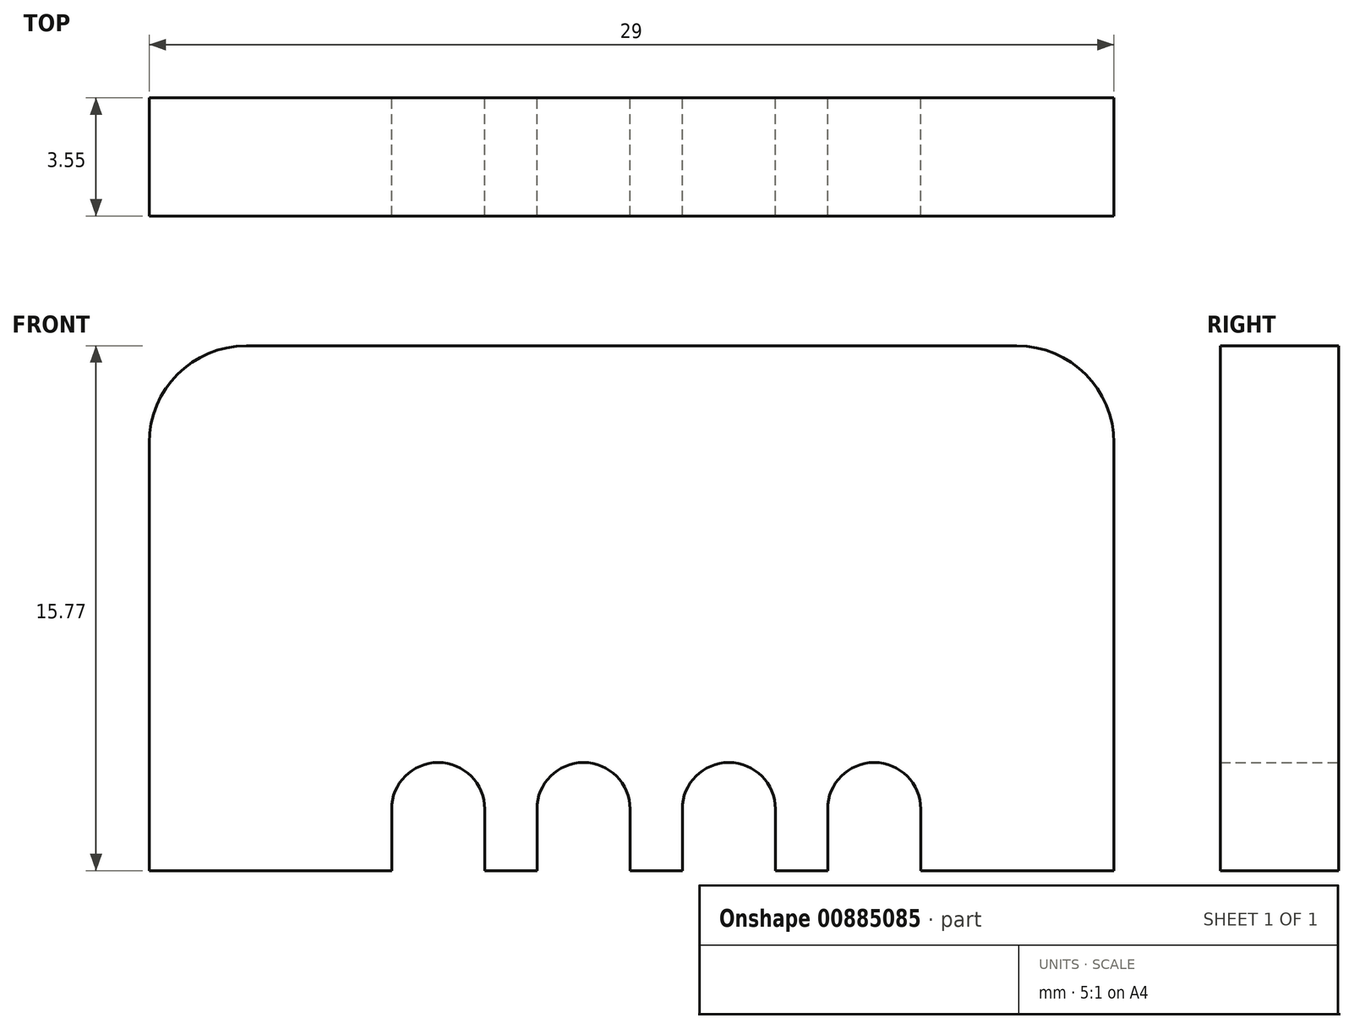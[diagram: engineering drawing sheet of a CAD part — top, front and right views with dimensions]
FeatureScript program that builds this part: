
annotation { "Feature Type Name" : "Feature", "Feature Type Description" : "" }
export const myFeature = defineFeature(function(context is Context, id is Id, definition is map)
    precondition{}
    {
        {
            var Q0;
            Q0=qCreatedBy(makeId("Front.planeOp"),FACE);
            var sketch = newSketch(context, id + "F0", { "sketchPlane" : qUnion([Q0])});
            skArc(sketch, "E0", {"start": v(-105.6, -27.46) * mm, "mid": v(-107.66, -28.32) * mm, "end": v(-108.52, -30.38) * mm});
            skArc(sketch, "E1", {"start": v(-108.52, -48.8) * mm, "mid": v(-107.66, -50.86) * mm, "end": v(-105.6, -51.72) * mm});
            skLineSegment(sketch, "E2", {"start": v(-105.6, -27.46) * mm, "end": v(-79.52, -27.46) * mm});
            skLineSegment(sketch, "E3", {"start": v(-79.52, -51.72) * mm, "end": v(-105.6, -51.72) * mm});
            skLineSegment(sketch, "E4", {"start": v(-108.52, -48.8) * mm, "end": v(-108.52, -30.38) * mm});
            skCircle(sketch, "E5", {"center": v(-99.83, -41.38) * mm, "radius": 1.4 * mm});
            skCircle(sketch, "E6", {"center": v(-95.46, -41.38) * mm, "radius": 1.4 * mm});
            skCircle(sketch, "E7", {"center": v(-91.1, -41.38) * mm, "radius": 1.4 * mm});
            skCircle(sketch, "E8", {"center": v(-86.73, -41.38) * mm, "radius": 1.4 * mm});
            skCircle(sketch, "E9", {"center": v(-102.02, -45.37) * mm, "radius": 1.4 * mm});
            skCircle(sketch, "E10", {"center": v(-97.65, -45.37) * mm, "radius": 1.4 * mm});
            skCircle(sketch, "E11", {"center": v(-93.28, -45.37) * mm, "radius": 1.4 * mm});
            skCircle(sketch, "E12", {"center": v(-88.91, -45.37) * mm, "radius": 1.4 * mm});
            skCircle(sketch, "E13", {"center": v(-76.58, -39.6) * mm, "radius": 1.6 * mm});
            skCircle(sketch, "E14", {"center": v(-76.58, -31.97) * mm, "radius": 1.2 * mm});
            skCircle(sketch, "E15", {"center": v(-76.58, -46.7) * mm, "radius": 1.2 * mm});
            skCircle(sketch, "E16", {"center": v(-76.58, -47.72) * mm, "radius": 1.2 * mm});
            skLineSegment(sketch, "E17", {"start": v(-79.52, -43.22) * mm, "end": v(-79.52, -51.72) * mm});
            skArc(sketch, "E18", {"start": v(-82.44, -51.72) * mm, "mid": v(-80.38, -50.86) * mm, "end": v(-79.52, -48.8) * mm});
            skLineSegment(sketch, "E19", {"start": v(-108.52, -43.52) * mm, "end": v(-74.05, -43.52) * mm});
            skLineSegment(sketch, "E20", {"start": v(-108.52, -43.23) * mm, "end": v(-74.04, -43.23) * mm});
            skLineSegment(sketch, "E21", {"start": v(-79.52, -43.22) * mm, "end": v(-79.52, -27.46) * mm});
            skArc(sketch, "E22", {"start": v(-79.52, -30.38) * mm, "mid": v(-80.38, -28.32) * mm, "end": v(-82.44, -27.46) * mm});
            skLineSegment(sketch, "E23", {"start": v(-110.85, -55.44) * mm, "end": v(-77.56, -55.44) * mm, "construction": true});
            skLineSegment(sketch, "E24.bottom", {"start": v(-103.42, -45.37) * mm, "end": v(-100.62, -45.37) * mm});
            skLineSegment(sketch, "E24.top", {"start": v(-103.42, -43.52) * mm, "end": v(-100.62, -43.52) * mm});
            skLineSegment(sketch, "E24.left", {"start": v(-103.42, -45.37) * mm, "end": v(-103.42, -43.52) * mm});
            skLineSegment(sketch, "E24.right", {"start": v(-100.62, -45.37) * mm, "end": v(-100.62, -43.52) * mm});
            skLineSegment(sketch, "E25.bottom", {"start": v(-99.05, -43.52) * mm, "end": v(-96.25, -43.52) * mm});
            skLineSegment(sketch, "E25.top", {"start": v(-99.05, -45.37) * mm, "end": v(-96.25, -45.37) * mm});
            skLineSegment(sketch, "E25.left", {"start": v(-99.05, -43.52) * mm, "end": v(-99.05, -45.37) * mm});
            skLineSegment(sketch, "E25.right", {"start": v(-96.25, -43.52) * mm, "end": v(-96.25, -45.37) * mm});
            skLineSegment(sketch, "E26.bottom", {"start": v(-94.68, -43.52) * mm, "end": v(-91.88, -43.52) * mm});
            skLineSegment(sketch, "E26.top", {"start": v(-94.68, -45.37) * mm, "end": v(-91.88, -45.37) * mm});
            skLineSegment(sketch, "E26.left", {"start": v(-94.68, -43.52) * mm, "end": v(-94.68, -45.37) * mm});
            skLineSegment(sketch, "E26.right", {"start": v(-91.88, -43.52) * mm, "end": v(-91.88, -45.37) * mm});
            skLineSegment(sketch, "E27.bottom", {"start": v(-90.31, -43.52) * mm, "end": v(-87.51, -43.52) * mm});
            skLineSegment(sketch, "E27.top", {"start": v(-90.31, -45.37) * mm, "end": v(-87.51, -45.37) * mm});
            skLineSegment(sketch, "E27.left", {"start": v(-90.31, -43.52) * mm, "end": v(-90.31, -45.37) * mm});
            skLineSegment(sketch, "E27.right", {"start": v(-87.51, -43.52) * mm, "end": v(-87.51, -45.37) * mm});
            skLineSegment(sketch, "E28.bottom", {"start": v(-101.23, -41.38) * mm, "end": v(-98.43, -41.38) * mm});
            skLineSegment(sketch, "E28.top", {"start": v(-101.23, -43.23) * mm, "end": v(-98.43, -43.23) * mm});
            skLineSegment(sketch, "E28.left", {"start": v(-101.23, -41.38) * mm, "end": v(-101.23, -43.23) * mm});
            skLineSegment(sketch, "E28.right", {"start": v(-98.43, -41.38) * mm, "end": v(-98.43, -43.23) * mm});
            skLineSegment(sketch, "E29.bottom", {"start": v(-96.86, -41.38) * mm, "end": v(-94.06, -41.38) * mm});
            skLineSegment(sketch, "E29.top", {"start": v(-96.86, -43.23) * mm, "end": v(-94.06, -43.23) * mm});
            skLineSegment(sketch, "E29.left", {"start": v(-96.86, -41.38) * mm, "end": v(-96.86, -43.23) * mm});
            skLineSegment(sketch, "E29.right", {"start": v(-94.06, -41.38) * mm, "end": v(-94.06, -43.23) * mm});
            skLineSegment(sketch, "E30.bottom", {"start": v(-92.5, -41.38) * mm, "end": v(-89.7, -41.38) * mm});
            skLineSegment(sketch, "E30.top", {"start": v(-92.5, -43.23) * mm, "end": v(-89.7, -43.23) * mm});
            skLineSegment(sketch, "E30.left", {"start": v(-92.5, -41.38) * mm, "end": v(-92.5, -43.23) * mm});
            skLineSegment(sketch, "E30.right", {"start": v(-89.7, -41.38) * mm, "end": v(-89.7, -43.23) * mm});
            skLineSegment(sketch, "E31.bottom", {"start": v(-88.13, -41.38) * mm, "end": v(-85.33, -41.38) * mm});
            skLineSegment(sketch, "E31.top", {"start": v(-88.13, -43.23) * mm, "end": v(-85.33, -43.23) * mm});
            skLineSegment(sketch, "E31.left", {"start": v(-88.13, -41.38) * mm, "end": v(-88.13, -43.23) * mm});
            skLineSegment(sketch, "E31.right", {"start": v(-85.33, -41.38) * mm, "end": v(-85.33, -43.23) * mm});
            skSolve(sketch);
        }
        {
            var Q0;
            {var subQ20=sQuery(id+"F0.wireOp",EDGE,"E0");Q0=makeQuery(id+"F0.imprint","IMPRINT",FACE,{"disambiguationData":[TD([[makeQuery(id+"F0.imprint","IMPRINT",EDGE,{"derivedFrom":subQ20}),1.0]])]});}
            extrude(context, id + "F1", {"entities" : qUnion([Q0]), "depth" : 3.55 * mm, "offsetDistance" : 25 * mm});
        }
    });
